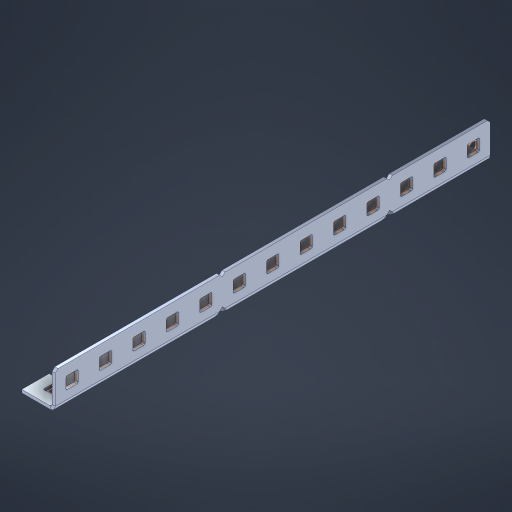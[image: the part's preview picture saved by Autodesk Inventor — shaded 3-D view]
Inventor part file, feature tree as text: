
AUTODESK INVENTOR PART (.ipt)
format: ipt  version: 2023 (Build 270158000, 158)  size: 748,544 bytes
history: native  units: in
note: dims shown in document units (in); Inventor stores cm internally (conversion verified against a paired STEP export)
features: other x46, extrude x37, sheet_metal_op x11, sketch x10, pattern_linear x2, mirror x1, chamfer x1
ambient origin geometry x8: Origin, YZ Plane, XZ Plane, XY Plane, X Axis, Y Axis, Z Axis, Center Point
bodies: Solid1 (feature_tree), Body (feature_tree)
feature tree (108):
  sheet_metal_op  "Flanges"
  other  "Flange Pattern Plane"
  other  "Flange Pattern Sketch"
  sheet_metal_op  "Flange Pattern"
  sheet_metal_op  "Body Pattern"
  pattern_linear  "Center Pattern"  Spacing1=0.0469in  [1 undecoded]
  other  "Arc Length"
  mirror  "Notch Mirror"
  pattern_linear  "Notch Pattern"  Spacing1=0.182in  [1 undecoded]
  chamfer  "End Chamfer"
  extrude  "Half Cut"  Depth=0.02in
  sketch  "Sketch1"  dims[d0=1.0in]
  other  "Plate1"
  sketch  "Sketch2"  dims[d1=6.5in]
  other  "Plate2"
  sheet_metal_op  "Bend1"
  sheet_metal_op  "Corner1"
  sketch  "Sketch3"  dims[d2=0.0469in]
  sketch  "Sketch7"  dims[d3=0.0469in]
  other  "Srf1"
  other  "Srf2"
  sketch  "Sketch8"  dims[d4=0.0234in]
  sketch  "Sketch9"  dims[d5=0.0938in]
  other  "Srf91"
  sheet_metal_op  "Body Pattern Sketch"
  other  "Srf92"
  sketch  "Sketch13"  dims[d6=0.0469in]
  sketch  "Sketch14"  dims[d7=0.5in d8=90.0deg d9=0.0312in]
  sketch  "Sketch15"  dims[d10=0.1875in]
  sketch  "Sketch16"  dims[d11=0.0469in d12=0.0469in d16=0.182in d17=0.02in d18=0.0469in d19=0.0in d20=0.25in d21=0.25in d38=5.1181in d40=0.5in d41=0.3937in d43=1.0in d46=0.172in d47=1.0in d48=0.0in d49=0.182in d50=0.02in d51=0.25in d52=0.25in d53=0.0469in d54=0.0in d55=0.172in d56=1.0in d57=0.0in d58=0.25in d60=5.1181in d62=0.5in d63=0.3937in d65=0.5in d85=0.1227in d86=0.1659in d88=0.04in d89=0.0469in d90=0.0in d91=0.04in d92=0.0491in d95=2.5in d96=0.04in d97=0.25in d98=45.0deg d99=0.25in d100=0.5in d101=0.0in d102=2.497in d106=0.182in d107=0.02in d108=0.5in d109=0.5in d110=0.0469in d111=0.0in d112=0.172in d113=0.5in d114=0.0in d117=0.5in d118=0.5in d119=0.5in]
  other  "Srf786"
  other  "Srf823"
  other  "Srf824"
  other  "Srf825"
  other  "Srf826"
  other  "Srf827"
  other  "Srf828"
  other  "Srf829"
  other  "Srf856"
  other  "Srf857"
  other  "Srf858"
  other  "Srf859"
  other  "Srf860"
  other  "Srf861"
  other  "Srf862"
  other  "Srf889"
  other  "Srf890"
  other  "Srf891"
  other  "Srf892"
  other  "Srf893"
  other  "Srf894"
  other  "Srf895"
  other  "Srf896"
  other  "Srf922"
  other  "Srf923"
  other  "Srf924"
  other  "Srf925"
  other  "Srf959"
  other  "Srf960"
  other  "Srf961"
  other  "Srf962"
  other  "Srf996"
  other  "Srf997"
  other  "Srf998"
  other  "Srf999"
  sheet_metal_op  "Flange Stamp"
  sheet_metal_op  "Flange Circle"
  sheet_metal_op  "Body Stamp"
  sheet_metal_op  "Body Circle"
  other  "Center Stamp"
  other  "Center Circle"
  sheet_metal_op  "Notch"
  extrude  "ExtrusionSrf2"  Depth=0.0469in
  extrude  "ExtrusionSrf92"  TaperAngle=0.0deg  [1 undecoded]
  extrude  "ExtrusionSrf823"  Depth=0.5in
  extrude  "ExtrusionSrf824"  Depth=0.5in
  extrude  "ExtrusionSrf825"  Depth=0.5in
  extrude  "ExtrusionSrf826"  Depth=0.5in
  extrude  "ExtrusionSrf827"  Depth=1.0in TaperAngle=0.0deg
  extrude  "ExtrusionSrf828"  Depth=0.182in
  extrude  "ExtrusionSrf829"  Depth=0.02in
  extrude  "ExtrusionSrf856"  Depth=0.5in
  extrude  "ExtrusionSrf857"  Depth=0.5in
  extrude  "ExtrusionSrf858"  Depth=0.0469in
  extrude  "ExtrusionSrf859"  TaperAngle=0.0deg  [1 undecoded]
  extrude  "ExtrusionSrf860"  Depth=0.5in
  extrude  "ExtrusionSrf861"  Depth=1.0in TaperAngle=0.0deg
  extrude  "ExtrusionSrf862"  Depth=0.5in
  extrude  "ExtrusionSrf889"  Depth=0.5in
  extrude  "ExtrusionSrf890"  Depth=0.5in
  extrude  "ExtrusionSrf891"  Depth=0.5in
  extrude  "ExtrusionSrf892"  Depth=0.5in
  extrude  "ExtrusionSrf893"  Depth=0.5in
  extrude  "ExtrusionSrf894"  Depth=0.0469in
  extrude  "ExtrusionSrf895"  TaperAngle=0.0deg  [1 undecoded]
  extrude  "ExtrusionSrf896"  Depth=0.5in
  extrude  "ExtrusionSrf922"  Depth=0.5in
  extrude  "ExtrusionSrf923"  Depth=2.5in
  extrude  "ExtrusionSrf924"  Depth=0.5in TaperAngle=45.0deg
  extrude  "ExtrusionSrf925"  Depth=0.5in
  extrude  "ExtrusionSrf959"  Depth=0.5in TaperAngle=0.0deg
  extrude  "ExtrusionSrf960"  Depth=0.5in
  extrude  "ExtrusionSrf961"  Depth=0.182in
  extrude  "ExtrusionSrf962"  Depth=0.02in
  extrude  "ExtrusionSrf996"  Depth=0.5in
  extrude  "ExtrusionSrf997"  Depth=0.5in
  extrude  "ExtrusionSrf998"  Depth=0.0469in
  extrude  "ExtrusionSrf999"  TaperAngle=0.0deg  [1 undecoded]
note: 6 required parameter values undecoded (feature->parameter linkage not recoverable at this tier; creation-order binding heuristic only, values carry confidence <= 0.55)
